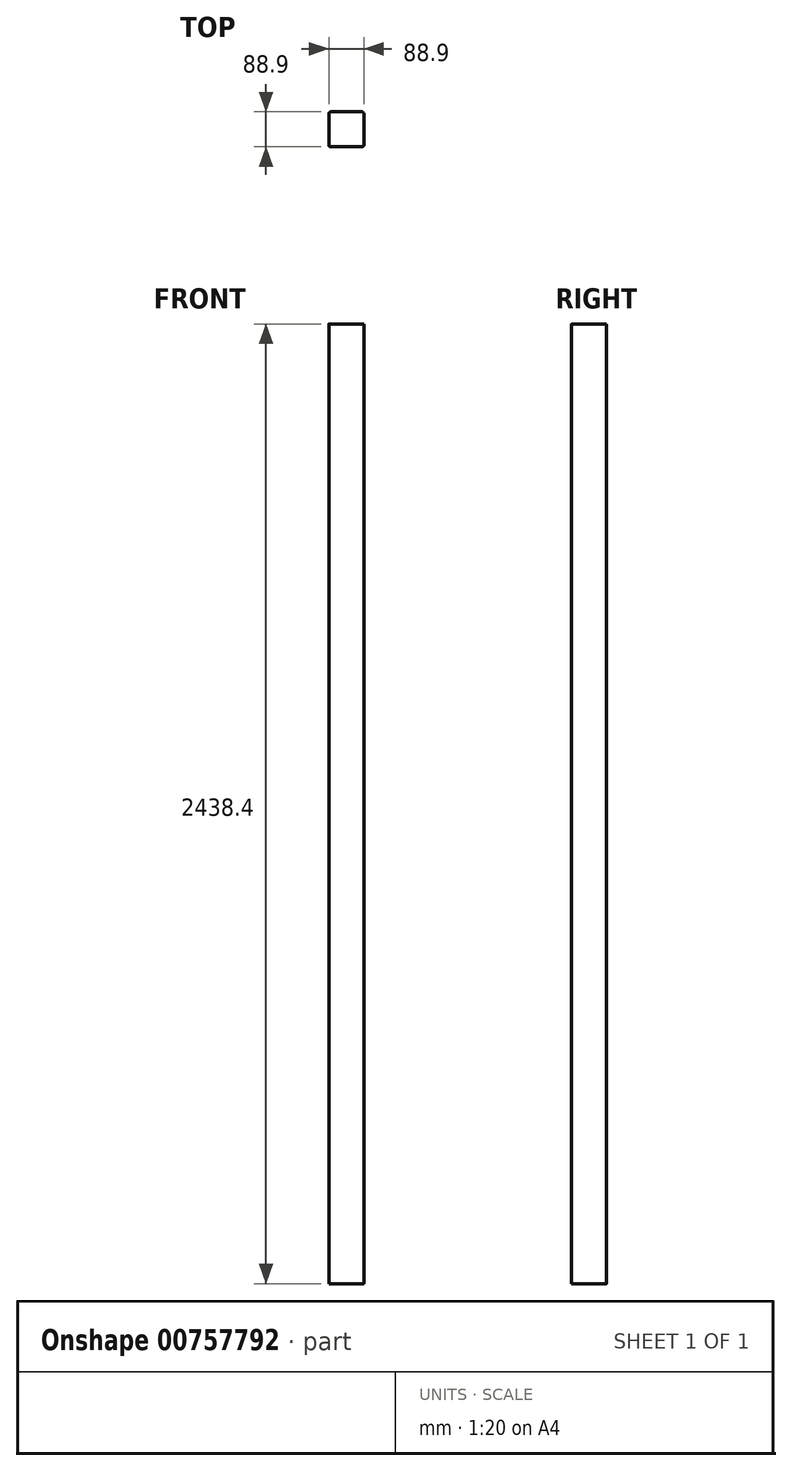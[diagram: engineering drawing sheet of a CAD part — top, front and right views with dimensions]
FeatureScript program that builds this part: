
annotation { "Feature Type Name" : "Feature", "Feature Type Description" : "" }
export const myFeature = defineFeature(function(context is Context, id is Id, definition is map)
    precondition{}
    {
        {
            var Q0;
            Q0=qCreatedBy(makeId("Top.planeOp"),FACE);
            var sketch = newSketch(context, id + "F0", { "sketchPlane" : qUnion([Q0])});
            skLineSegment(sketch, "E0.bottom", {"start": v(-42.32, 44.04) * mm, "end": v(46.58, 44.04) * mm});
            skLineSegment(sketch, "E0.top", {"start": v(-42.32, -44.86) * mm, "end": v(46.58, -44.86) * mm});
            skLineSegment(sketch, "E0.left", {"start": v(-42.32, 44.04) * mm, "end": v(-42.32, -44.86) * mm});
            skLineSegment(sketch, "E0.right", {"start": v(46.58, 44.04) * mm, "end": v(46.58, -44.86) * mm});
            skSolve(sketch);
        }
        {
            var Q0;
            Q0=makeQuery(id+"F0.imprint","IMPRINT",FACE,{"disambiguationData":[TD([[makeQuery(id+"F0.imprint","IMPRINT",EDGE,{"derivedFrom":sQuery(id+"F0.wireOp",EDGE,"E0.bottom")}),-1.0]])]});
            extrude(context, id + "F1", {"entities" : qUnion([Q0]), "depth" : 2438.4 * mm, "offsetDistance" : 25.4 * mm});
        }
        {
            var Q0;
            Q0=makeQuery(id+"F1.opExtrude","SWEPT_EDGE",EDGE,{"disambiguationData":[OSD([sQuery(id+"F0.wireOp",EDGE,"E0.bottom"),sQuery(id+"F0.wireOp",EDGE,"E0.left")])]});
            var Q1;
            Q1=makeQuery(id+"F1.opExtrude","SWEPT_EDGE",EDGE,{"disambiguationData":[OSD([sQuery(id+"F0.wireOp",EDGE,"E0.top"),sQuery(id+"F0.wireOp",EDGE,"E0.left")])]});
            var Q2;
            Q2=makeQuery(id+"F1.opExtrude","SWEPT_EDGE",EDGE,{"disambiguationData":[OSD([sQuery(id+"F0.wireOp",EDGE,"E0.bottom"),sQuery(id+"F0.wireOp",EDGE,"E0.right")])]});
            var Q3;
            Q3=makeQuery(id+"F1.opExtrude","SWEPT_EDGE",EDGE,{"disambiguationData":[OSD([sQuery(id+"F0.wireOp",EDGE,"E0.top"),sQuery(id+"F0.wireOp",EDGE,"E0.right")])]});
            fillet(context, id + "F2", {"entities" : qUnion([Q0, Q1, Q2, Q3]), "radius" : 5.08 * mm, "tangentPropagation" : true, "allowEdgeOverflow" : false});
        }
    });
